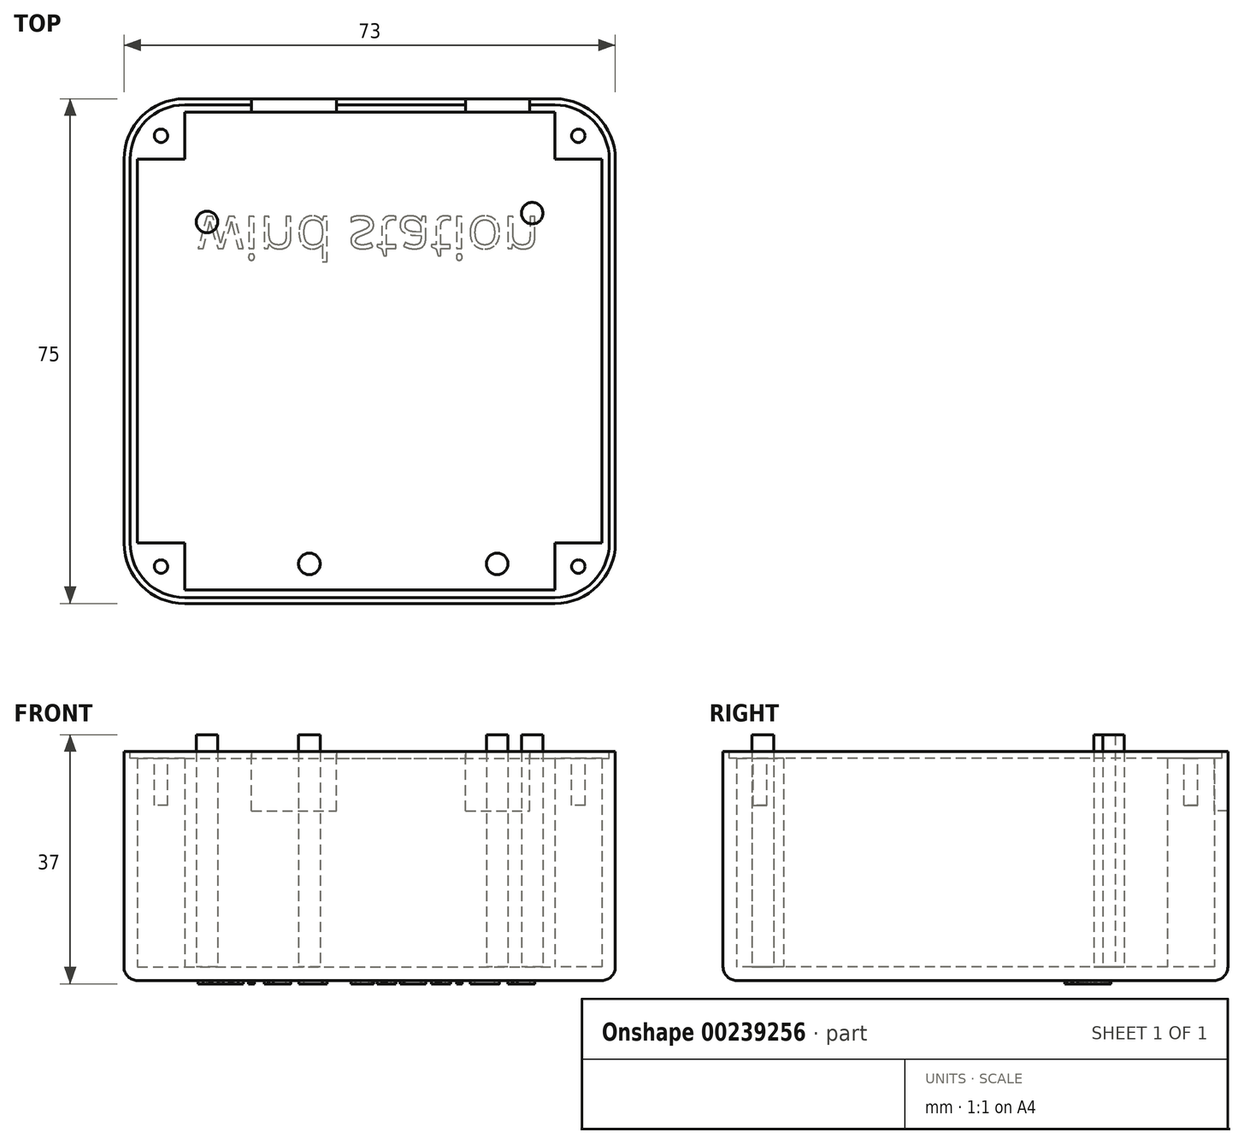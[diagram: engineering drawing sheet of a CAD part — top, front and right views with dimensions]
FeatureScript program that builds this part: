
annotation { "Feature Type Name" : "Feature", "Feature Type Description" : "" }
export const myFeature = defineFeature(function(context is Context, id is Id, definition is map)
    precondition{}
    {
        {
            var Q0;
            Q0=qCreatedBy(makeId("Top.planeOp"),FACE);
            var sketch = newSketch(context, id + "F0", { "sketchPlane" : qUnion([Q0])});
            skLineSegment(sketch, "E0.bottom", {"start": v(-27.5, 38.5) * mm, "end": v(27.5, 38.5) * mm});
            skLineSegment(sketch, "E0.top", {"start": v(-27.5, -36.5) * mm, "end": v(27.5, -36.5) * mm});
            skLineSegment(sketch, "E0.left", {"start": v(-36.5, 29.5) * mm, "end": v(-36.5, -27.5) * mm});
            skLineSegment(sketch, "E0.right", {"start": v(36.5, 29.5) * mm, "end": v(36.5, -27.5) * mm});
            skPoint(sketch, "E1.visualSharp", {"position": v(-36.5, 38.5) * mm});
            skArc(sketch, "E1.filletArc", {"start": v(-27.5, 38.5) * mm, "mid": v(-33.86, 35.86) * mm, "end": v(-36.5, 29.5) * mm});
            skPoint(sketch, "E2.visualSharp", {"position": v(36.5, 38.5) * mm});
            skArc(sketch, "E2.filletArc", {"start": v(36.5, 29.5) * mm, "mid": v(33.86, 35.86) * mm, "end": v(27.5, 38.5) * mm});
            skPoint(sketch, "E3.visualSharp", {"position": v(36.5, -36.5) * mm});
            skArc(sketch, "E3.filletArc", {"start": v(27.5, -36.5) * mm, "mid": v(33.86, -33.86) * mm, "end": v(36.5, -27.5) * mm});
            skPoint(sketch, "E4.visualSharp", {"position": v(-36.5, -36.5) * mm});
            skArc(sketch, "E4.filletArc", {"start": v(-36.5, -27.5) * mm, "mid": v(-33.86, -33.86) * mm, "end": v(-27.5, -36.5) * mm});
            skSolve(sketch);
        }
        {
            var Q0;
            Q0=qSketchRegion(id+"F0",true);
            extrude(context, id + "F1", {"entities" : qUnion([Q0]), "depth" : 2 * mm});
        }
        {
            var Q0;
            Q0=makeQuery(id+"F1.opExtrude","CAP_FACE",FACE,{"disambiguationData":[OSD([sQuery(id+"F0.wireOp",EDGE,"E0.bottom"),sQuery(id+"F0.wireOp",EDGE,"E0.top"),sQuery(id+"F0.wireOp",EDGE,"E0.left"),sQuery(id+"F0.wireOp",EDGE,"E0.right"),sQuery(id+"F0.wireOp",EDGE,"E1.filletArc"),sQuery(id+"F0.wireOp",EDGE,"E2.filletArc"),sQuery(id+"F0.wireOp",EDGE,"E3.filletArc"),sQuery(id+"F0.wireOp",EDGE,"E4.filletArc")])],"isStart":false});
            var sketch = newSketch(context, id + "F2", { "sketchPlane" : qUnion([Q0])});
            skCircle(sketch, "E5.MirrorC", {"center": v(-24.16, 20.2) * mm, "radius": 1.6 * mm});
            skCircle(sketch, "E6.MirrorC", {"center": v(24.14, 21.5) * mm, "radius": 1.6 * mm});
            skCircle(sketch, "E7.MirrorC", {"center": v(18.94, -30.6) * mm, "radius": 1.6 * mm});
            skCircle(sketch, "E8.MirrorC", {"center": v(-8.96, -30.6) * mm, "radius": 1.6 * mm});
            skSolve(sketch);
        }
        {
            var Q0;
            Q0=qSketchRegion(id+"F2",true);
            extrude(context, id + "F3", {"entities" : qUnion([Q0]), "operationType" : NewBodyOperationType.ADD, "depth" : 34.5 * mm});
        }
        {
            var Q0;
            Q0=makeQuery(id+"F1.opExtrude","CAP_FACE",FACE,{"disambiguationData":[OSD([sQuery(id+"F0.wireOp",EDGE,"E0.bottom"),sQuery(id+"F0.wireOp",EDGE,"E0.top"),sQuery(id+"F0.wireOp",EDGE,"E0.left"),sQuery(id+"F0.wireOp",EDGE,"E0.right"),sQuery(id+"F0.wireOp",EDGE,"E1.filletArc"),sQuery(id+"F0.wireOp",EDGE,"E2.filletArc"),sQuery(id+"F0.wireOp",EDGE,"E3.filletArc"),sQuery(id+"F0.wireOp",EDGE,"E4.filletArc")])],"isStart":false});
            var sketch = newSketch(context, id + "F4", { "sketchPlane" : qUnion([Q0])});
            skLineSegment(sketch, "E9", {"start": v(-27.5, 36.5) * mm, "end": v(27.5, 36.5) * mm});
            skLineSegment(sketch, "E10", {"start": v(-34.5, 29.5) * mm, "end": v(-34.5, -27.5) * mm});
            skLineSegment(sketch, "E11", {"start": v(-27.5, -34.5) * mm, "end": v(27.5, -34.5) * mm});
            skLineSegment(sketch, "E12", {"start": v(34.5, -27.5) * mm, "end": v(34.5, 29.5) * mm});
            skArc(sketch, "E13", {"start": v(-27.5, 36.5) * mm, "mid": v(-32.45, 34.45) * mm, "end": v(-34.5, 29.5) * mm});
            skArc(sketch, "E14", {"start": v(27.5, -34.5) * mm, "mid": v(32.45, -32.45) * mm, "end": v(34.5, -27.5) * mm});
            skArc(sketch, "E15", {"start": v(-34.5, -27.5) * mm, "mid": v(-32.45, -32.45) * mm, "end": v(-27.5, -34.5) * mm});
            skArc(sketch, "E16", {"start": v(34.5, 29.5) * mm, "mid": v(32.45, 34.45) * mm, "end": v(27.5, 36.5) * mm});
            skLineSegment(sketch, "E17.0", {"start": v(-27.5, 38.5) * mm, "end": v(27.5, 38.5) * mm});
            skArc(sketch, "E17.1", {"start": v(36.5, 29.5) * mm, "mid": v(33.86, 35.86) * mm, "end": v(27.5, 38.5) * mm});
            skLineSegment(sketch, "E17.2", {"start": v(36.5, 29.5) * mm, "end": v(36.5, -27.5) * mm});
            skArc(sketch, "E17.3", {"start": v(27.5, -36.5) * mm, "mid": v(33.86, -33.86) * mm, "end": v(36.5, -27.5) * mm});
            skLineSegment(sketch, "E17.4", {"start": v(-27.5, -36.5) * mm, "end": v(27.5, -36.5) * mm});
            skArc(sketch, "E17.5", {"start": v(-36.5, -27.5) * mm, "mid": v(-33.86, -33.86) * mm, "end": v(-27.5, -36.5) * mm});
            skLineSegment(sketch, "E17.6", {"start": v(-36.5, 29.5) * mm, "end": v(-36.5, -27.5) * mm});
            skArc(sketch, "E17.7", {"start": v(-27.5, 38.5) * mm, "mid": v(-33.86, 35.86) * mm, "end": v(-36.5, 29.5) * mm});
            skSolve(sketch);
        }
        {
            var Q0;
            Q0=qSketchRegion(id+"F4",true);
            extrude(context, id + "F5", {"entities" : qUnion([Q0]), "operationType" : NewBodyOperationType.ADD, "depth" : 32 * mm});
        }
        {
            var Q0;
            Q0=makeQuery(id+"F5.opExtrude","CAP_FACE",FACE,{"disambiguationData":[OSD([sQuery(id+"F4.wireOp",EDGE,"E9"),sQuery(id+"F4.wireOp",EDGE,"E10"),sQuery(id+"F4.wireOp",EDGE,"E11"),sQuery(id+"F4.wireOp",EDGE,"E12"),sQuery(id+"F4.wireOp",EDGE,"E13"),sQuery(id+"F4.wireOp",EDGE,"E14"),sQuery(id+"F4.wireOp",EDGE,"E15"),sQuery(id+"F4.wireOp",EDGE,"E16"),sQuery(id+"F4.wireOp",EDGE,"E17.0"),sQuery(id+"F4.wireOp",EDGE,"E17.1"),sQuery(id+"F4.wireOp",EDGE,"E17.2"),sQuery(id+"F4.wireOp",EDGE,"E17.3"),sQuery(id+"F4.wireOp",EDGE,"E17.4"),sQuery(id+"F4.wireOp",EDGE,"E17.5"),sQuery(id+"F4.wireOp",EDGE,"E17.6"),sQuery(id+"F4.wireOp",EDGE,"E17.7")])],"isStart":false});
            var sketch = newSketch(context, id + "F6", { "sketchPlane" : qUnion([Q0])});
            skLineSegment(sketch, "E18", {"start": v(-27.5, 37.6) * mm, "end": v(27.5, 37.6) * mm});
            skLineSegment(sketch, "E19", {"start": v(-27.5, -35.6) * mm, "end": v(27.5, -35.6) * mm});
            skLineSegment(sketch, "E20", {"start": v(-35.6, 29.5) * mm, "end": v(-35.6, -27.5) * mm});
            skLineSegment(sketch, "E21", {"start": v(35.6, 29.5) * mm, "end": v(35.6, -27.5) * mm});
            skLineSegment(sketch, "E22.0", {"start": v(-27.5, 36.5) * mm, "end": v(27.5, 36.5) * mm});
            skArc(sketch, "E22.1", {"start": v(34.5, 29.5) * mm, "mid": v(32.45, 34.45) * mm, "end": v(27.5, 36.5) * mm});
            skLineSegment(sketch, "E22.2", {"start": v(34.5, -27.5) * mm, "end": v(34.5, 29.5) * mm});
            skArc(sketch, "E22.3", {"start": v(27.5, -34.5) * mm, "mid": v(32.45, -32.45) * mm, "end": v(34.5, -27.5) * mm});
            skLineSegment(sketch, "E22.4", {"start": v(-27.5, -34.5) * mm, "end": v(27.5, -34.5) * mm});
            skArc(sketch, "E22.5", {"start": v(-34.5, -27.5) * mm, "mid": v(-32.45, -32.45) * mm, "end": v(-27.5, -34.5) * mm});
            skLineSegment(sketch, "E22.6", {"start": v(-34.5, 29.5) * mm, "end": v(-34.5, -27.5) * mm});
            skArc(sketch, "E22.7", {"start": v(-27.5, 36.5) * mm, "mid": v(-32.45, 34.45) * mm, "end": v(-34.5, 29.5) * mm});
            skArc(sketch, "E23", {"start": v(-27.5, 37.6) * mm, "mid": v(-33.23, 35.23) * mm, "end": v(-35.6, 29.5) * mm});
            skArc(sketch, "E24", {"start": v(35.6, 29.5) * mm, "mid": v(33.23, 35.23) * mm, "end": v(27.5, 37.6) * mm});
            skArc(sketch, "E25", {"start": v(27.5, -35.6) * mm, "mid": v(33.23, -33.23) * mm, "end": v(35.6, -27.5) * mm});
            skArc(sketch, "E26", {"start": v(-35.6, -27.5) * mm, "mid": v(-33.23, -33.23) * mm, "end": v(-27.5, -35.6) * mm});
            skSolve(sketch);
        }
        {
            var Q0;
            Q0=qSketchRegion(id+"F6",true);
            extrude(context, id + "F7", {"entities" : qUnion([Q0]), "operationType" : NewBodyOperationType.REMOVE, "oppositeDirection" : true, "depth" : 1 * mm});
        }
        {
            var Q0;
            Q0=makeQuery(id+"F5.opExtrude","CAP_FACE",FACE,{"disambiguationData":[OSD([sQuery(id+"F4.wireOp",EDGE,"E9"),sQuery(id+"F4.wireOp",EDGE,"E10"),sQuery(id+"F4.wireOp",EDGE,"E11"),sQuery(id+"F4.wireOp",EDGE,"E12"),sQuery(id+"F4.wireOp",EDGE,"E13"),sQuery(id+"F4.wireOp",EDGE,"E14"),sQuery(id+"F4.wireOp",EDGE,"E15"),sQuery(id+"F4.wireOp",EDGE,"E16"),sQuery(id+"F4.wireOp",EDGE,"E17.0"),sQuery(id+"F4.wireOp",EDGE,"E17.1"),sQuery(id+"F4.wireOp",EDGE,"E17.2"),sQuery(id+"F4.wireOp",EDGE,"E17.3"),sQuery(id+"F4.wireOp",EDGE,"E17.4"),sQuery(id+"F4.wireOp",EDGE,"E17.5"),sQuery(id+"F4.wireOp",EDGE,"E17.6"),sQuery(id+"F4.wireOp",EDGE,"E17.7")])],"isStart":false});
            var sketch = newSketch(context, id + "F8", { "sketchPlane" : qUnion([Q0])});
            skLineSegment(sketch, "E27.bottom", {"start": v(-17.56, 38.5) * mm, "end": v(-4.96, 38.5) * mm});
            skLineSegment(sketch, "E27.top", {"start": v(-17.56, 36.5) * mm, "end": v(-4.96, 36.5) * mm});
            skLineSegment(sketch, "E27.left", {"start": v(-17.56, 38.5) * mm, "end": v(-17.56, 36.5) * mm});
            skLineSegment(sketch, "E27.right", {"start": v(-4.96, 38.5) * mm, "end": v(-4.96, 36.5) * mm});
            skLineSegment(sketch, "E28.bottom", {"start": v(14.24, 38.5) * mm, "end": v(23.74, 38.5) * mm});
            skLineSegment(sketch, "E28.top", {"start": v(14.24, 36.5) * mm, "end": v(23.74, 36.5) * mm});
            skLineSegment(sketch, "E28.left", {"start": v(14.24, 38.5) * mm, "end": v(14.24, 36.5) * mm});
            skLineSegment(sketch, "E28.right", {"start": v(23.74, 38.5) * mm, "end": v(23.74, 36.5) * mm});
            skSolve(sketch);
        }
        {
            var Q0;
            Q0=qSketchRegion(id+"F8",true);
            extrude(context, id + "F9", {"entities" : qUnion([Q0]), "operationType" : NewBodyOperationType.REMOVE, "oppositeDirection" : true, "depth" : 8.8 * mm});
        }
        {
            var Q0;
            Q0=makeQuery(id+"F1.opExtrude","CAP_FACE",FACE,{"disambiguationData":[OSD([sQuery(id+"F0.wireOp",EDGE,"E0.bottom"),sQuery(id+"F0.wireOp",EDGE,"E0.top"),sQuery(id+"F0.wireOp",EDGE,"E0.left"),sQuery(id+"F0.wireOp",EDGE,"E0.right"),sQuery(id+"F0.wireOp",EDGE,"E1.filletArc"),sQuery(id+"F0.wireOp",EDGE,"E2.filletArc"),sQuery(id+"F0.wireOp",EDGE,"E3.filletArc"),sQuery(id+"F0.wireOp",EDGE,"E4.filletArc")])],"isStart":false});
            var sketch = newSketch(context, id + "F10", { "sketchPlane" : qUnion([Q0])});
            skLineSegment(sketch, "E29", {"start": v(-27.5, 36.5) * mm, "end": v(-27.5, 29.5) * mm});
            skLineSegment(sketch, "E30", {"start": v(-27.5, 29.5) * mm, "end": v(-34.5, 29.5) * mm});
            skArc(sketch, "E31.0", {"start": v(-27.5, 36.5) * mm, "mid": v(-32.45, 34.45) * mm, "end": v(-34.5, 29.5) * mm});
            skArc(sketch, "E31.1", {"start": v(34.5, 29.5) * mm, "mid": v(32.45, 34.45) * mm, "end": v(27.5, 36.5) * mm});
            skArc(sketch, "E31.2", {"start": v(27.5, -34.5) * mm, "mid": v(32.45, -32.45) * mm, "end": v(34.5, -27.5) * mm});
            skArc(sketch, "E31.3", {"start": v(-34.5, -27.5) * mm, "mid": v(-32.45, -32.45) * mm, "end": v(-27.5, -34.5) * mm});
            skLineSegment(sketch, "E32", {"start": v(-34.5, -27.5) * mm, "end": v(-27.5, -27.5) * mm});
            skLineSegment(sketch, "E33", {"start": v(-27.5, -27.5) * mm, "end": v(-27.5, -34.5) * mm});
            skLineSegment(sketch, "E34", {"start": v(34.5, -27.5) * mm, "end": v(27.5, -27.5) * mm});
            skLineSegment(sketch, "E35", {"start": v(27.5, -34.5) * mm, "end": v(27.5, -27.5) * mm});
            skLineSegment(sketch, "E36", {"start": v(27.5, 36.5) * mm, "end": v(27.5, 29.5) * mm});
            skLineSegment(sketch, "E37", {"start": v(34.5, 29.5) * mm, "end": v(27.5, 29.5) * mm});
            skSolve(sketch);
        }
        {
            var Q0;
            Q0=qSketchRegion(id+"F10",true);
            extrude(context, id + "F11", {"entities" : qUnion([Q0]), "operationType" : NewBodyOperationType.ADD, "depth" : 31 * mm});
        }
        {
            var Q0;
            {var subQ0=sQuery(id+"F6.wireOp",EDGE,"E18");var subQ1=sQuery(id+"F6.wireOp",EDGE,"E19");var subQ2=sQuery(id+"F6.wireOp",EDGE,"E20");var subQ3=sQuery(id+"F6.wireOp",EDGE,"E21");var subQ4=sQuery(id+"F6.wireOp",EDGE,"E23");var subQ5=sQuery(id+"F6.wireOp",EDGE,"E24");var subQ6=sQuery(id+"F6.wireOp",EDGE,"E25");var subQ7=sQuery(id+"F6.wireOp",EDGE,"E26");Q0=makeQuery(id+"F11.boolean.opBoolean","MERGE",FACE,{"derivedFrom":[makeQuery(id+"F9.boolean.opBoolean","SPLIT",FACE,{"disambiguationData":[TD([makeQuery(id+"F5.opExtrude","SWEPT_FACE",FACE,{"disambiguationData":[OSD([sQuery(id+"F4.wireOp",EDGE,"E10")])]})])],"derivedFrom":makeQuery(id+"F7.boolean.opBoolean","COPY",FACE,{"derivedFrom":makeQuery(id+"F7.opExtrude","CAP_FACE",FACE,{"disambiguationData":[OSD([subQ0,subQ1,subQ2,subQ3,sQuery(id+"F6.wireOp",EDGE,"E22.0"),sQuery(id+"F6.wireOp",EDGE,"E22.1"),sQuery(id+"F6.wireOp",EDGE,"E22.2"),sQuery(id+"F6.wireOp",EDGE,"E22.3"),sQuery(id+"F6.wireOp",EDGE,"E22.4"),sQuery(id+"F6.wireOp",EDGE,"E22.5"),sQuery(id+"F6.wireOp",EDGE,"E22.6"),sQuery(id+"F6.wireOp",EDGE,"E22.7"),subQ4,subQ5,subQ6,subQ7])],"isStart":false})})}),makeQuery(id+"F11.opExtrude","CAP_FACE",FACE,{"disambiguationData":[OSD([sQuery(id+"F10.wireOp",EDGE,"E29"),sQuery(id+"F10.wireOp",EDGE,"E30"),sQuery(id+"F10.wireOp",EDGE,"E31.0")])],"isStart":false}),makeQuery(id+"F11.opExtrude","CAP_FACE",FACE,{"disambiguationData":[OSD([sQuery(id+"F10.wireOp",EDGE,"E31.1"),sQuery(id+"F10.wireOp",EDGE,"E36"),sQuery(id+"F10.wireOp",EDGE,"E37")])],"isStart":false}),makeQuery(id+"F11.opExtrude","CAP_FACE",FACE,{"disambiguationData":[OSD([sQuery(id+"F10.wireOp",EDGE,"E31.2"),sQuery(id+"F10.wireOp",EDGE,"E34"),sQuery(id+"F10.wireOp",EDGE,"E35")])],"isStart":false}),makeQuery(id+"F11.opExtrude","CAP_FACE",FACE,{"disambiguationData":[OSD([sQuery(id+"F10.wireOp",EDGE,"E31.3"),sQuery(id+"F10.wireOp",EDGE,"E32"),sQuery(id+"F10.wireOp",EDGE,"E33")])],"isStart":false})]});}
            var sketch = newSketch(context, id + "F12", { "sketchPlane" : qUnion([Q0])});
            skCircle(sketch, "E38", {"center": v(-31, 33) * mm, "radius": 1 * mm});
            skCircle(sketch, "E39", {"center": v(31, 33) * mm, "radius": 1 * mm});
            skCircle(sketch, "E40", {"center": v(31, -31) * mm, "radius": 1 * mm});
            skCircle(sketch, "E41", {"center": v(-31, -31) * mm, "radius": 1 * mm});
            skSolve(sketch);
        }
        {
            var Q0;
            Q0=qSketchRegion(id+"F12",true);
            extrude(context, id + "F13", {"entities" : qUnion([Q0]), "operationType" : NewBodyOperationType.REMOVE, "oppositeDirection" : true, "depth" : 7 * mm});
        }
        {
            var Q0;
            Q0=makeQuery(id+"F1.opExtrude","CAP_EDGE",EDGE,{"disambiguationData":[OSD([sQuery(id+"F0.wireOp",EDGE,"E0.bottom")])],"isStart":true});
            fillet(context, id + "F14", {"entities" : qUnion([Q0]), "radius" : 2 * mm, "tangentPropagation" : true, "allowEdgeOverflow" : false});
        }
        {
            var Q0;
            Q0=makeQuery(id+"F1.opExtrude","CAP_FACE",FACE,{"disambiguationData":[OSD([sQuery(id+"F0.wireOp",EDGE,"E0.bottom"),sQuery(id+"F0.wireOp",EDGE,"E0.top"),sQuery(id+"F0.wireOp",EDGE,"E0.left"),sQuery(id+"F0.wireOp",EDGE,"E0.right"),sQuery(id+"F0.wireOp",EDGE,"E1.filletArc"),sQuery(id+"F0.wireOp",EDGE,"E2.filletArc"),sQuery(id+"F0.wireOp",EDGE,"E3.filletArc"),sQuery(id+"F0.wireOp",EDGE,"E4.filletArc")])],"isStart":true});
            var sketch = newSketch(context, id + "F15", { "sketchPlane" : qUnion([Q0])});
            skText(sketch, "E42", { "text": "wind station\n", "fontName": "OpenSans-Regular.ttf"});
            const initialGuessF15  = {"E42": [-0.02559, -0.02102, 1, 0, 0.00639]};
            skSetInitialGuess(sketch, initialGuessF15);
            skSolve(sketch);
        }
        {
            var Q0;
            Q0 = qSketchRegion(id + "F15", true);
            extrude(context, id + "F16", {"entities" : qUnion([Q0]), "operationType" : NewBodyOperationType.ADD, "depth" : 0.5 * mm});
        }
    });
